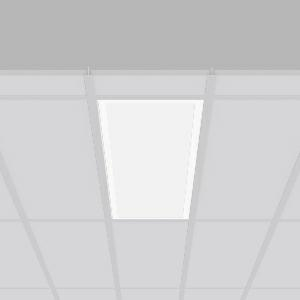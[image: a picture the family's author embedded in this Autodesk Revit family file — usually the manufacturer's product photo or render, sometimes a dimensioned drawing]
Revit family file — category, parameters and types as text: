
# Revit family: sidelite_eco_672378_002_07_2071
name_source: partatom
category: Lighting Fixtures
units: mm (PartAtom-declared; Revit-internal decimal feet)

## family parameters
Cut with Voids When Loaded = No
Host = Face
Light Source = No
Part Type = Normal
Room Calculation Point = No
Round Connector Dimension = Use Diameter
Shared = No

## types (1)
- SIDELITE ECO (1 x LED Modul 830, 3300 lm, 3000)
    Apparent Load = 29 VA
    CIE Flux Codes = 47 79 96 100 100
    Color Rendering = 80
    Color Temperature = 3000
    Default Elevation = 1800 mm
    Description = Series: SIDELITE ECO
Highly economical recessed luminaire with progressive LED technology. For escape route illumination. Frame made of aluminium, powder-coated. Diffuser: plastic, opal. Lightguide and diffuser made of non-yellowing plastic (PMMA). Lateral light emission (RZB SIDELITE technology) for homogeneous light distribution. External driver. Self-contained system with automatic self-test and feedback via DALI bus, only to RZB DALI monitoring system. External driver with simple plug-in locking system. Extended connection cable (1.90 m). 
Colour: white
Length: 1245 mm
Width: 308 mm
Cut-out length: 1220 mm
Cut-out width: 285 mm
Recess height: 160 mm
Luminaire: recess height: 40 mm
Weight: 4.7 kg
Operating mode: maintained power mode
Duration time: 8 h
Lamp: LED
Socket: without socket
Colour temperature: 3000K
Colour rendering index (CRI): 80
System power: 29 W
Rated luminous flux: 3300 lm
Luminous flux, emergency: 220 lm
System power, emergency: -
Control gear: Regulated power supply
Protection class: I
Type of protection: IP 40
    Height = 0 mm  [stored 0 ft]
    Lamp = 1 x LED Modul 830
    Lamp Light Flux = 3300 lm
    Lamp count = 1
    Length = 1245 mm
    Lifetime = 50000 h
    Luminous efficacy = 114 lm/W
    Manufacturer = RZB
    ModVariant = No
    Model = 672378.002.07
    Mounting Place = Ceiling
    Mounting Type = Recessed
    Number of Poles = 1
    OnlyDefault = Yes
    Power Factor = 1
    Product Name = SIDELITE ECO
    Product group = Recessed modular luminaires
    ProductGroupID = 406
    Protection Class = Protection class I
    Protection Degree = IP 40
    RLX_Detail_Level = 1
    RLX_Emergency_Light_Flux = 220 lm
    RLX_Emergency_Type = 3
    RLX_Emergency_Type_DB = Yes
    RlxData = <blob elided: 30125 chars, md5=a53968c2>
    Socket = socket
    Standby Power = 0 W
    System Light Flux = 3300 lm
    System Power = 29 W
    Type Comments = Product without accessories
    Type Image = 312367.002.jpg
    URL = http://relux.com
    VarID = ---
    Voltage = 230 V
    Voltage Range = 220-240 V
    Weight = 0.00 kg
    Width = 308 mm

note: [stored X ft] marks values corroborated as IEEE doubles in the binary element streams (Revit-internal decimal feet)

## geometry (parser evidence)
native form markers: Blend x4, Sweep x10
no freeform markers — native parametric forms only
